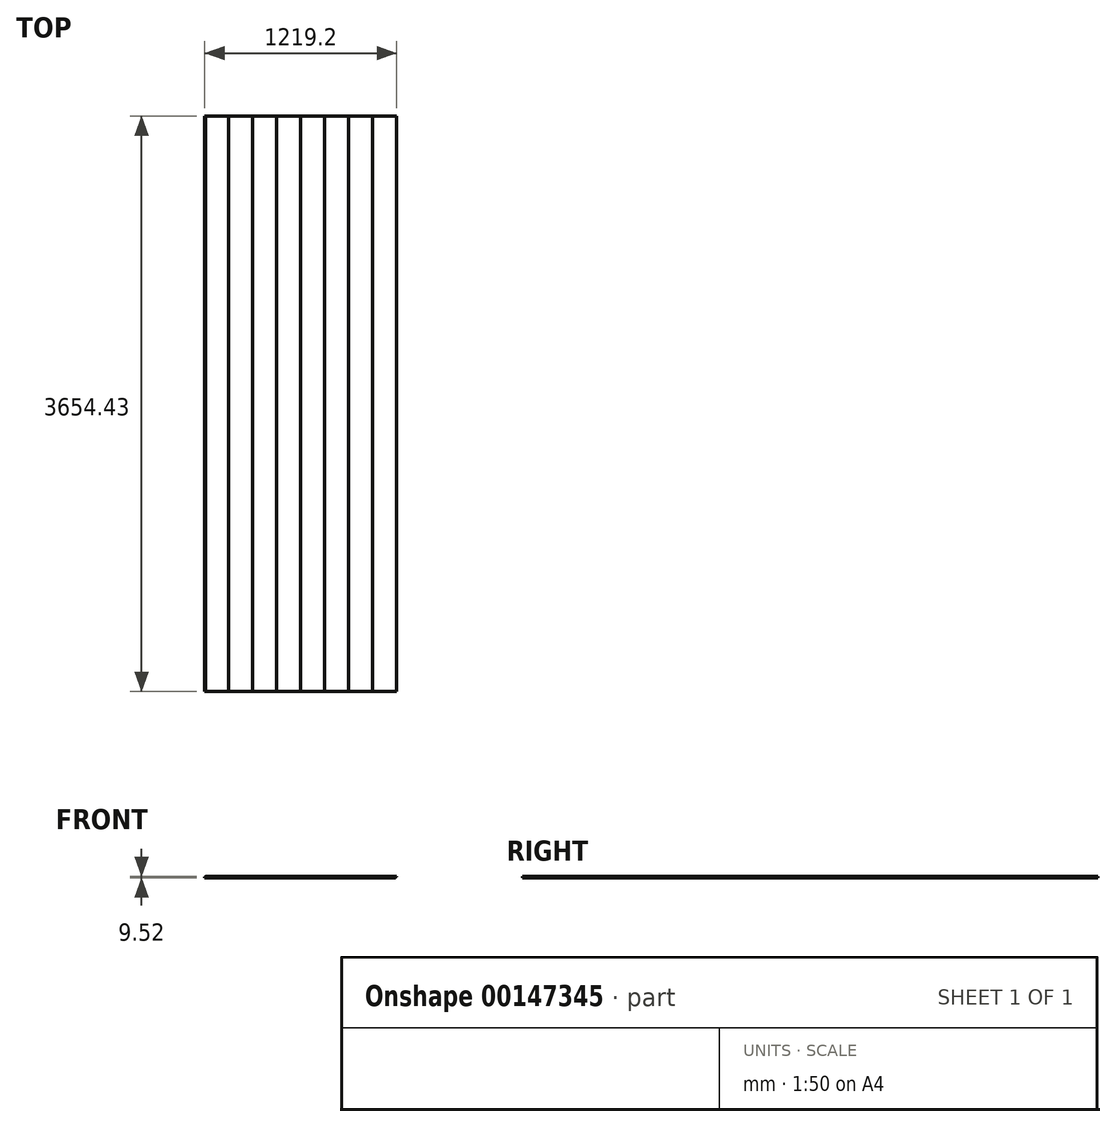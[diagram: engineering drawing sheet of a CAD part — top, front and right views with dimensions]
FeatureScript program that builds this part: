
annotation { "Feature Type Name" : "Feature", "Feature Type Description" : "" }
export const myFeature = defineFeature(function(context is Context, id is Id, definition is map)
    precondition{}
    {
        {
            var Q0;
            Q0=qCreatedBy(makeId("Top.planeOp"),FACE);
            var sketch = newSketch(context, id + "F0", { "sketchPlane" : qUnion([Q0])});
            skLineSegment(sketch, "E0.bottom", {"start": v(-609.6, 3130.65) * mm, "end": v(609.6, 3130.65) * mm});
            skLineSegment(sketch, "E0.top", {"start": v(-609.6, -523.78) * mm, "end": v(609.6, -523.78) * mm});
            skLineSegment(sketch, "E0.left", {"start": v(-609.6, 3130.65) * mm, "end": v(-609.6, -523.78) * mm});
            skLineSegment(sketch, "E0.right", {"start": v(609.6, 3130.65) * mm, "end": v(609.6, -523.78) * mm});
            skSolve(sketch);
        }
        {
            var Q0;
            Q0=qSketchRegion(id+"F0",true);
            extrude(context, id + "F1", {"entities" : qUnion([Q0]), "endBound" : BoundingType.SYMMETRIC, "depth" : 9.52 * mm});
        }
        {
            var Q0;
            Q0=makeQuery(id+"F1.opExtrude","SWEPT_FACE",FACE,{"disambiguationData":[OSD([sQuery(id+"F0.wireOp",EDGE,"E0.top")])]});
            var sketch = newSketch(context, id + "F2", { "sketchPlane" : qUnion([Q0])});
            skLineSegment(sketch, "E1", {"start": v(609.6, 0) * mm, "end": v(603.25, 0) * mm});
            skPoint(sketch, "E1.endSnap0", {"position": v(609.6, 0) * mm});
            skLineSegment(sketch, "E2", {"start": v(603.25, 0) * mm, "end": v(603.25, -4.76) * mm});
            skLineSegment(sketch, "E3", {"start": v(609.6, 0) * mm, "end": v(609.6, -4.76) * mm});
            skLineSegment(sketch, "E4", {"start": v(609.6, -4.76) * mm, "end": v(603.25, -4.76) * mm});
            skLineSegment(sketch, "E5.bottom", {"start": v(-609.6, 4.76) * mm, "end": v(-603.25, 4.76) * mm});
            skLineSegment(sketch, "E5.top", {"start": v(-609.6, 0) * mm, "end": v(-603.25, 0) * mm});
            skLineSegment(sketch, "E5.left", {"start": v(-609.6, 4.76) * mm, "end": v(-609.6, 0) * mm});
            skLineSegment(sketch, "E5.right", {"start": v(-603.25, 4.76) * mm, "end": v(-603.25, 0) * mm});
            skSolve(sketch);
        }
        {
            var Q0;
            Q0=qSketchRegion(id+"F2",true);
            extrude(context, id + "F3", {"entities" : qUnion([Q0]), "operationType" : NewBodyOperationType.REMOVE, "endBound" : BoundingType.THROUGH_ALL, "oppositeDirection" : true, "depth" : 25.4 * mm});
        }
        {
            var Q0;
            Q0=makeQuery(id+"F1.opExtrude","SWEPT_FACE",FACE,{"disambiguationData":[OSD([sQuery(id+"F0.wireOp",EDGE,"E0.top")])]});
            var sketch = newSketch(context, id + "F4", { "sketchPlane" : qUnion([Q0])});
            skLineSegment(sketch, "E6.bottom", {"start": v(-458, 4.76) * mm, "end": v(-456.4, 4.76) * mm});
            skLineSegment(sketch, "E6.top", {"start": v(-458, 3.17) * mm, "end": v(-456.4, 3.17) * mm});
            skLineSegment(sketch, "E6.left", {"start": v(-458, 4.76) * mm, "end": v(-458, 3.17) * mm});
            skLineSegment(sketch, "E6.right", {"start": v(-456.4, 4.76) * mm, "end": v(-456.4, 3.17) * mm});
            skPoint(sketch, "E7", {"position": v(-457.2, 3.17) * mm});
            skPoint(sketch, "E8.1.0.0", {"position": v(-304.8, 3.17) * mm});
            skLineSegment(sketch, "E8.1.0.1", {"start": v(-305.6, 4.76) * mm, "end": v(-304, 4.76) * mm});
            skLineSegment(sketch, "E8.1.0.2", {"start": v(-305.6, 3.17) * mm, "end": v(-304, 3.17) * mm});
            skLineSegment(sketch, "E8.1.0.3", {"start": v(-305.6, 4.76) * mm, "end": v(-305.6, 3.17) * mm});
            skLineSegment(sketch, "E8.1.0.4", {"start": v(-304, 4.76) * mm, "end": v(-304, 3.17) * mm});
            skPoint(sketch, "E8.2.0.0", {"position": v(-152.4, 3.17) * mm});
            skLineSegment(sketch, "E8.2.0.1", {"start": v(-153.2, 4.76) * mm, "end": v(-151.6, 4.76) * mm});
            skLineSegment(sketch, "E8.2.0.2", {"start": v(-153.2, 3.17) * mm, "end": v(-151.6, 3.17) * mm});
            skLineSegment(sketch, "E8.2.0.3", {"start": v(-153.2, 4.76) * mm, "end": v(-153.2, 3.17) * mm});
            skLineSegment(sketch, "E8.2.0.4", {"start": v(-151.6, 4.76) * mm, "end": v(-151.6, 3.17) * mm});
            skPoint(sketch, "E8.3.0.0", {"position": v(0, 3.17) * mm});
            skLineSegment(sketch, "E8.3.0.1", {"start": v(-0.8, 4.76) * mm, "end": v(0.8, 4.76) * mm});
            skLineSegment(sketch, "E8.3.0.2", {"start": v(-0.8, 3.17) * mm, "end": v(0.8, 3.17) * mm});
            skLineSegment(sketch, "E8.3.0.3", {"start": v(-0.8, 4.76) * mm, "end": v(-0.8, 3.17) * mm});
            skLineSegment(sketch, "E8.3.0.4", {"start": v(0.8, 4.76) * mm, "end": v(0.8, 3.17) * mm});
            skPoint(sketch, "E8.4.0.0", {"position": v(152.4, 3.17) * mm});
            skLineSegment(sketch, "E8.4.0.1", {"start": v(151.6, 4.76) * mm, "end": v(153.2, 4.76) * mm});
            skLineSegment(sketch, "E8.4.0.2", {"start": v(151.6, 3.17) * mm, "end": v(153.2, 3.17) * mm});
            skLineSegment(sketch, "E8.4.0.3", {"start": v(151.6, 4.76) * mm, "end": v(151.6, 3.17) * mm});
            skLineSegment(sketch, "E8.4.0.4", {"start": v(153.2, 4.76) * mm, "end": v(153.2, 3.17) * mm});
            skPoint(sketch, "E8.5.0.0", {"position": v(304.8, 3.17) * mm});
            skLineSegment(sketch, "E8.5.0.1", {"start": v(304, 4.76) * mm, "end": v(305.6, 4.76) * mm});
            skLineSegment(sketch, "E8.5.0.2", {"start": v(304, 3.17) * mm, "end": v(305.6, 3.17) * mm});
            skLineSegment(sketch, "E8.5.0.3", {"start": v(304, 4.76) * mm, "end": v(304, 3.17) * mm});
            skLineSegment(sketch, "E8.5.0.4", {"start": v(305.6, 4.76) * mm, "end": v(305.6, 3.17) * mm});
            skPoint(sketch, "E8.6.0.0", {"position": v(457.2, 3.17) * mm});
            skLineSegment(sketch, "E8.6.0.1", {"start": v(456.4, 4.76) * mm, "end": v(458, 4.76) * mm});
            skLineSegment(sketch, "E8.6.0.2", {"start": v(456.4, 3.17) * mm, "end": v(458, 3.17) * mm});
            skLineSegment(sketch, "E8.6.0.3", {"start": v(456.4, 4.76) * mm, "end": v(456.4, 3.17) * mm});
            skLineSegment(sketch, "E8.6.0.4", {"start": v(458, 4.76) * mm, "end": v(458, 3.17) * mm});
            skLineSegment(sketch, "E8.direction1", {"start": v(-457.2, 3.17) * mm, "end": v(-304.8, 3.17) * mm, "construction": true});
            skSolve(sketch);
        }
        {
            var Q0;
            Q0=qSketchRegion(id+"F4",true);
            extrude(context, id + "F5", {"entities" : qUnion([Q0]), "operationType" : NewBodyOperationType.REMOVE, "endBound" : BoundingType.THROUGH_ALL, "oppositeDirection" : true, "depth" : 25.4 * mm});
        }
    });
